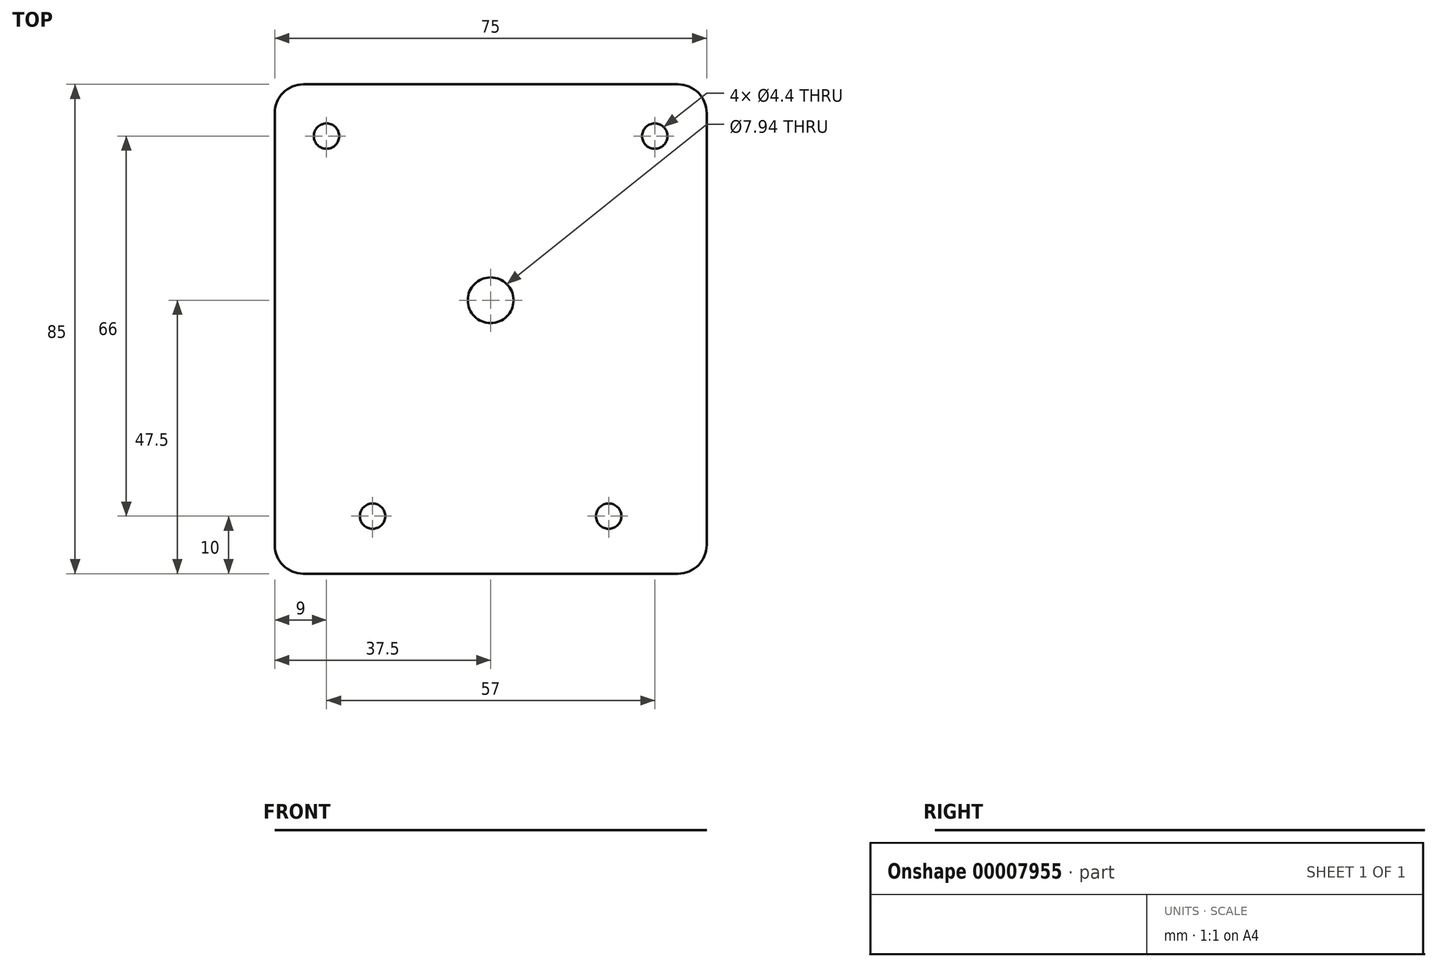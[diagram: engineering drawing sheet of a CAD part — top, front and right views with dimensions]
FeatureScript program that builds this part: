
annotation { "Feature Type Name" : "Feature", "Feature Type Description" : "" }
export const myFeature = defineFeature(function(context is Context, id is Id, definition is map)
    precondition{}
    {
        {
            var Q0;
            Q0=qCreatedBy(makeId("Top.planeOp"),FACE);
            var sketch = newSketch(context, id + "F0", { "sketchPlane" : qUnion([Q0])});
            skLineSegment(sketch, "E0.bottom", {"start": v(0, 0) * mm, "end": v(75, 0) * mm});
            skLineSegment(sketch, "E0.top", {"start": v(0, 85) * mm, "end": v(75, 85) * mm});
            skLineSegment(sketch, "E0.left", {"start": v(0, 0) * mm, "end": v(0, 85) * mm});
            skLineSegment(sketch, "E0.right", {"start": v(75, 0) * mm, "end": v(75, 85) * mm});
            skCircle(sketch, "E1", {"center": v(9, 76) * mm, "radius": 2.2 * mm});
            skCircle(sketch, "E2", {"center": v(17, 10) * mm, "radius": 2.2 * mm});
            skLineSegment(sketch, "E3", {"start": v(37.5, 85) * mm, "end": v(37.5, 0) * mm, "construction": true});
            skCircle(sketch, "E4", {"center": v(37.5, 47.5) * mm, "radius": 3.97 * mm});
            skLineSegment(sketch, "E5", {"start": v(37.5, 47.5) * mm, "end": v(37.5, 85) * mm, "construction": true});
            skLineSegment(sketch, "E6", {"start": v(37.5, 47.5) * mm, "end": v(0, 47.5) * mm, "construction": true});
            skCircle(sketch, "E7.0.MirrorC", {"center": v(58, 10) * mm, "radius": 2.2 * mm});
            skCircle(sketch, "E8.0.MirrorC", {"center": v(66, 76) * mm, "radius": 2.2 * mm});
            skSolve(sketch);
        }
        {
            var Q0;
            Q0 = qSketchRegion(id + "F0", true);
            extrude(context, id + "F1", {"entities" : qUnion([Q0]), "depth" : 1 / 203.2 * mm});
        }
        {
            var Q0;
            Q0=makeQuery(id+"F1.opExtrude","SWEPT_EDGE",EDGE,{"disambiguationData":[OSD([sQuery(id+"F0.wireOp",EDGE,"E0.bottom"),sQuery(id+"F0.wireOp",EDGE,"E0.left")])]});
            var Q1;
            Q1=makeQuery(id+"F1.opExtrude","SWEPT_EDGE",EDGE,{"disambiguationData":[OSD([sQuery(id+"F0.wireOp",EDGE,"E0.top"),sQuery(id+"F0.wireOp",EDGE,"E0.right")])]});
            var Q2;
            Q2=makeQuery(id+"F1.opExtrude","SWEPT_EDGE",EDGE,{"disambiguationData":[OSD([sQuery(id+"F0.wireOp",EDGE,"E0.bottom"),sQuery(id+"F0.wireOp",EDGE,"E0.right")])]});
            var Q3;
            Q3=makeQuery(id+"F1.opExtrude","SWEPT_EDGE",EDGE,{"disambiguationData":[OSD([sQuery(id+"F0.wireOp",EDGE,"E0.top"),sQuery(id+"F0.wireOp",EDGE,"E0.left")])]});
            fillet(context, id + "F2", {"entities" : qUnion([Q0, Q1, Q2, Q3]), "radius" : 5 * mm, "tangentPropagation" : true, "allowEdgeOverflow" : false});
        }
    });
